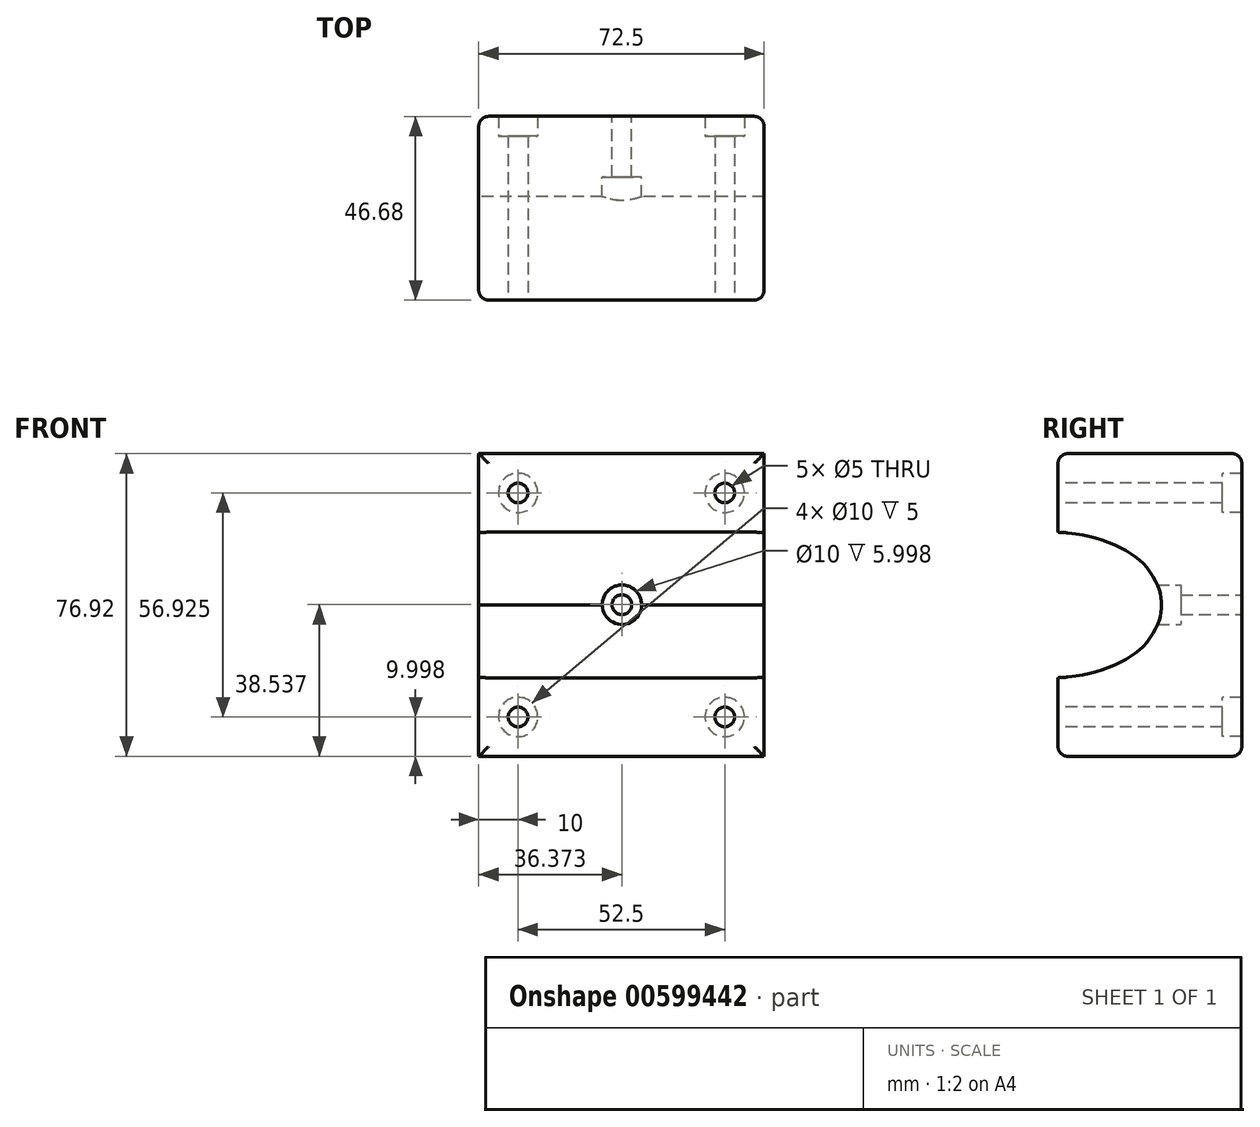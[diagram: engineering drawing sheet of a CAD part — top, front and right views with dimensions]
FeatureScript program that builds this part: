
annotation { "Feature Type Name" : "Feature", "Feature Type Description" : "" }
export const myFeature = defineFeature(function(context is Context, id is Id, definition is map)
    precondition{}
    {
        {
            var Q0;
            Q0=qCreatedBy(makeId("Right.planeOp"),FACE);
            var sketch = newSketch(context, id + "F0", { "sketchPlane" : qUnion([Q0])});
            skFitSpline(sketch, "E0.0", {"points": [v(-65.87, 0.89) * mm, v(-64.8, 1.67) * mm, v(-62.45, 3.19) * mm, v(-57.02, 6.06) * mm, v(-50.73, 8.67) * mm, v(-44.06, 10.98) * mm, v(-38.98, 12.54) * mm, v(-33.97, 13.9) * mm, v(-27.45, 15.46) * mm, v(-21.18, 16.65) * mm, v(-15.26, 17.5) * mm, v(-11.02, 18) * mm, v(-7, 18.34) * mm, v(-3.2, 18.55) * mm, v(0.4, 18.66) * mm, v(3.25, 18.68) * mm, v(5.47, 18.65) * mm, v(7.1, 18.62) * mm, v(8.7, 18.58) * mm, v(10.8, 18.5) * mm, v(13.41, 18.32) * mm, v(15.98, 18.01) * mm, v(18.01, 17.64) * mm, v(19.53, 17.3) * mm, v(21.04, 16.88) * mm, v(22.99, 16.25) * mm, v(24.85, 15.51) * mm, v(26.59, 14.7) * mm, v(27.81, 14.07) * mm, v(28.95, 13.42) * mm, v(30, 12.76) * mm, v(30.96, 12.06) * mm, v(31.85, 11.32) * mm, v(32.68, 10.52) * mm, v(33.46, 9.67) * mm, v(34.18, 8.74) * mm, v(34.86, 7.74) * mm, v(35.5, 6.7) * mm, v(36.05, 5.65) * mm, v(36.44, 4.76) * mm, v(36.7, 4.05) * mm, v(36.88, 3.52) * mm, v(37.01, 3) * mm, v(37.15, 2.32) * mm, v(37.25, 1.54) * mm, v(37.3, 0.7) * mm, v(37.3, 0.22) * mm, v(37.3, 0) * mm]});
            skLineSegment(sketch, "E1", {"start": v(11.06, 18.47) * mm, "end": v(11.06, 38.46) * mm});
            skLineSegment(sketch, "E2", {"start": v(11.06, 38.46) * mm, "end": v(57.74, 38.46) * mm});
            skFitSpline(sketch, "E3.MirrorCS", {"points": [v(-65.87, -0.89) * mm, v(-64.8, -1.67) * mm, v(-62.45, -3.19) * mm, v(-57.02, -6.06) * mm, v(-50.73, -8.67) * mm, v(-44.06, -10.98) * mm, v(-38.98, -12.54) * mm, v(-33.97, -13.9) * mm, v(-27.45, -15.46) * mm, v(-21.18, -16.65) * mm, v(-15.26, -17.5) * mm, v(-11.02, -18) * mm, v(-7, -18.34) * mm, v(-3.2, -18.55) * mm, v(0.4, -18.66) * mm, v(3.25, -18.68) * mm, v(5.47, -18.65) * mm, v(7.1, -18.62) * mm, v(8.7, -18.58) * mm, v(10.8, -18.5) * mm, v(13.41, -18.32) * mm, v(15.98, -18.01) * mm, v(18.01, -17.64) * mm, v(19.53, -17.3) * mm, v(21.04, -16.88) * mm, v(22.99, -16.25) * mm, v(24.85, -15.51) * mm, v(26.59, -14.7) * mm, v(27.81, -14.07) * mm, v(28.95, -13.42) * mm, v(30, -12.76) * mm, v(30.96, -12.06) * mm, v(31.85, -11.32) * mm, v(32.68, -10.52) * mm, v(33.46, -9.67) * mm, v(34.18, -8.74) * mm, v(34.86, -7.74) * mm, v(35.5, -6.7) * mm, v(36.05, -5.65) * mm, v(36.44, -4.76) * mm, v(36.7, -4.05) * mm, v(36.88, -3.52) * mm, v(37.01, -3) * mm, v(37.15, -2.32) * mm, v(37.25, -1.54) * mm, v(37.3, -0.7) * mm, v(37.3, -0.22) * mm, v(37.3, 0) * mm]});
            skLineSegment(sketch, "E4.MirrorCS", {"start": v(11.06, -38.46) * mm, "end": v(57.74, -38.46) * mm});
            skLineSegment(sketch, "E5.MirrorCS", {"start": v(11.06, -18.47) * mm, "end": v(11.06, -38.46) * mm});
            skLineSegment(sketch, "E6", {"start": v(57.74, 38.46) * mm, "end": v(57.74, -38.46) * mm});
            skSolve(sketch);
        }
        {
            var Q0;
            Q0 = qSketchRegion(id + "F0", true);
            extrude(context, id + "F1", {"entities" : qUnion([Q0]), "depth" : 72.5 * mm, "offsetDistance" : 25 * mm});
        }
        {
            var Q0;
            Q0=makeQuery(id+"F1.opExtrude","SWEPT_FACE",FACE,{"disambiguationData":[OSD([sQuery(id+"F0.wireOp",EDGE,"E1")])]});
            var sketch = newSketch(context, id + "F2", { "sketchPlane" : qUnion([Q0])});
            skPoint(sketch, "E7", {"position": v(36.37, 0.08) * mm});
            skSolve(sketch);
        }
        {
            var Q0;
            Q0=sQuery(id+"F2.wireOp",VERTEX,"8a5668b4-76ee-41ec-8645-79288d4d8dce");
            var Q1;
            Q1=sQuery(id+"F2.wireOp",VERTEX,"E7");
            var Q2;
            Q2=makeQuery(id+"F1.opExtrude","SWEPT_BODY",BODY,{"disambiguationData":[OSD([sQuery(id+"F0.wireOp",EDGE,"E0.0"),sQuery(id+"F0.wireOp",EDGE,"E1"),sQuery(id+"F0.wireOp",EDGE,"E2"),sQuery(id+"F0.wireOp",EDGE,"E3.MirrorCS"),sQuery(id+"F0.wireOp",EDGE,"E4.MirrorCS"),sQuery(id+"F0.wireOp",EDGE,"E5.MirrorCS"),sQuery(id+"F0.wireOp",EDGE,"E6")])]});
            hole(context, id + "F3", {"style" : HoleStyle.C_BORE, "endStyle" : HoleEndStyle.THROUGH, "holeDiameter" : 5 * mm, "cBoreDiameter" : 10 * mm, "cBoreDepth" : 5 * mm, "majorDiameter" : 5 * mm, "isTappedThrough" : true, "tappedDepth" : 12 * mm, "tapClearance" : 3, "locations" : qUnion([Q0, Q1]), "scope" : qUnion([Q2]), "startStyle" : HoleStartStyle.PART});
        }
        {
            var Q0;
            Q0=makeQuery(id+"F1.opExtrude","SWEPT_FACE",FACE,{"disambiguationData":[OSD([sQuery(id+"F0.wireOp",EDGE,"E6")])]});
            var sketch = newSketch(context, id + "F4", { "sketchPlane" : qUnion([Q0])});
            skSolve(sketch);
        }
        {
            var Q0;
            Q0=makeQuery(id+"F1.opExtrude","SWEPT_EDGE",EDGE,{"disambiguationData":[OSD([sQuery(id+"F0.wireOp",EDGE,"E4.MirrorCS"),sQuery(id+"F0.wireOp",EDGE,"E6")])]});
            var Q1;
            Q1=makeQuery(id+"F1.opExtrude","CAP_EDGE",EDGE,{"disambiguationData":[OSD([sQuery(id+"F0.wireOp",EDGE,"E6")])],"isStart":false});
            var Q2;
            Q2=makeQuery(id+"F1.opExtrude","SWEPT_EDGE",EDGE,{"disambiguationData":[OSD([sQuery(id+"F0.wireOp",EDGE,"E2"),sQuery(id+"F0.wireOp",EDGE,"E6")])]});
            var Q3;
            Q3=makeQuery(id+"F1.opExtrude","CAP_EDGE",EDGE,{"disambiguationData":[OSD([sQuery(id+"F0.wireOp",EDGE,"E6")])],"isStart":true});
            fillet(context, id + "F5", {"entities" : qUnion([Q0, Q1, Q2, Q3]), "radius" : 2.5 * mm, "tangentPropagation" : true, "allowEdgeOverflow" : false});
        }
        {
            var Q0;
            Q0=makeQuery(id+"F1.opExtrude","CAP_EDGE",EDGE,{"disambiguationData":[OSD([sQuery(id+"F0.wireOp",EDGE,"E1")])],"isStart":true});
            var Q1;
            Q1=makeQuery(id+"F1.opExtrude","SWEPT_EDGE",EDGE,{"disambiguationData":[OSD([sQuery(id+"F0.wireOp",EDGE,"E1"),sQuery(id+"F0.wireOp",EDGE,"E2")])]});
            var Q2;
            Q2=makeQuery(id+"F1.opExtrude","CAP_EDGE",EDGE,{"disambiguationData":[OSD([sQuery(id+"F0.wireOp",EDGE,"E1")])],"isStart":false});
            var Q3;
            Q3=makeQuery(id+"F1.opExtrude","CAP_EDGE",EDGE,{"disambiguationData":[OSD([sQuery(id+"F0.wireOp",EDGE,"E5.MirrorCS")])],"isStart":false});
            var Q4;
            Q4=makeQuery(id+"F1.opExtrude","SWEPT_EDGE",EDGE,{"disambiguationData":[OSD([sQuery(id+"F0.wireOp",EDGE,"E4.MirrorCS"),sQuery(id+"F0.wireOp",EDGE,"E5.MirrorCS")])]});
            var Q5;
            Q5=makeQuery(id+"F1.opExtrude","CAP_EDGE",EDGE,{"disambiguationData":[OSD([sQuery(id+"F0.wireOp",EDGE,"E5.MirrorCS")])],"isStart":true});
            fillet(context, id + "F6", {"entities" : qUnion([Q0, Q1, Q2, Q3, Q4, Q5]), "radius" : 2.5 * mm, "tangentPropagation" : true, "allowEdgeOverflow" : false});
        }
        {
            var Q0;
            {var subQ0=sQuery(id+"F0.wireOp",EDGE,"E6");Q0=makeQuery(id+"F4.imprint","IMPRINT",FACE,{"disambiguationData":[TD([[makeQuery(id+"F4.imprint","IMPRINT",EDGE,{"derivedFrom":makeQuery(id+"F1.opExtrude","CAP_EDGE",EDGE,{"disambiguationData":[OSD([subQ0])],"isStart":true})}),-1.0]])]});}
            var sketch = newSketch(context, id + "F7", { "sketchPlane" : qUnion([Q0])});
            skLineSegment(sketch, "E8", {"start": v(-87.6, 28.46) * mm, "end": v(9.67, 28.46) * mm});
            skLineSegment(sketch, "E9", {"start": v(-62.5, 42.62) * mm, "end": v(-62.5, -45.8) * mm});
            skPoint(sketch, "E10", {"position": v(-62.5, 28.46) * mm});
            skLineSegment(sketch, "E11", {"start": v(-10, 50.15) * mm, "end": v(-10, -46.25) * mm});
            skLineSegment(sketch, "E12", {"start": v(-91.74, -28.46) * mm, "end": v(11.22, -28.46) * mm});
            skPoint(sketch, "E13", {"position": v(-10, 28.46) * mm});
            skPoint(sketch, "E14", {"position": v(-62.5, -28.46) * mm});
            skPoint(sketch, "E15", {"position": v(-10, -28.46) * mm});
            skSolve(sketch);
        }
        {
            var Q0;
            Q0=sQuery(id+"F7.wireOp",VERTEX,"E10");
            var Q1;
            Q1=sQuery(id+"F7.wireOp",VERTEX,"E13");
            var Q2;
            Q2=sQuery(id+"F7.wireOp",VERTEX,"E14");
            var Q3;
            Q3=sQuery(id+"F7.wireOp",VERTEX,"E15");
            var Q4;
            Q4=makeQuery(id+"F1.opExtrude","SWEPT_BODY",BODY,{"disambiguationData":[OSD([sQuery(id+"F0.wireOp",EDGE,"E0.0"),sQuery(id+"F0.wireOp",EDGE,"E1"),sQuery(id+"F0.wireOp",EDGE,"E2"),sQuery(id+"F0.wireOp",EDGE,"E3.MirrorCS"),sQuery(id+"F0.wireOp",EDGE,"E4.MirrorCS"),sQuery(id+"F0.wireOp",EDGE,"E5.MirrorCS"),sQuery(id+"F0.wireOp",EDGE,"E6")])]});
            hole(context, id + "F8", {"style" : HoleStyle.C_BORE, "endStyle" : HoleEndStyle.THROUGH, "holeDiameter" : 5 * mm, "cBoreDiameter" : 10 * mm, "cBoreDepth" : 5 * mm, "majorDiameter" : 5 * mm, "isTappedThrough" : true, "tappedDepth" : 12 * mm, "tapClearance" : 3, "locations" : qUnion([Q0, Q1, Q2, Q3]), "scope" : qUnion([Q4]), "startStyle" : HoleStartStyle.PART});
        }
    });
